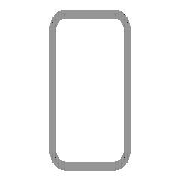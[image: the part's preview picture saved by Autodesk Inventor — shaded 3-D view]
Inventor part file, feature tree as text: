
AUTODESK INVENTOR PART (.ipt)
format: ipt  version: 2025 (Build 290162010, 162A)  size: 133,632 bytes
history: native  units: mm (DEFAULTED — no unit token found)
features: other x4, sketch x1, plane x1
ambient origin geometry x8: Origin, YZ Plane, XZ Plane, XY Plane, X Axis, Y Axis, Z Axis, Center Point
bodies: Solid1 (feature_tree), Body (feature_tree)
feature tree (6):
  parser-record x1  (decoder bookkeeping rows leaked as tree rows — omitted from the tree; the rows remain in map.json)
  other  "Driven Length"
  other  "Start Plane"
  other  "End Plane"
  sketch  "Sketch3"  dims[d3=960.0mm d4=0.0mm d7=6.0mm d9=20.0mm d11=40.0mm d12=3.0mm d13=20.0mm d14=980.0mm d15=10.0mm d16=20.0mm d17=90.0deg d18=960.0mm]
  plane  "Work Plane3"
